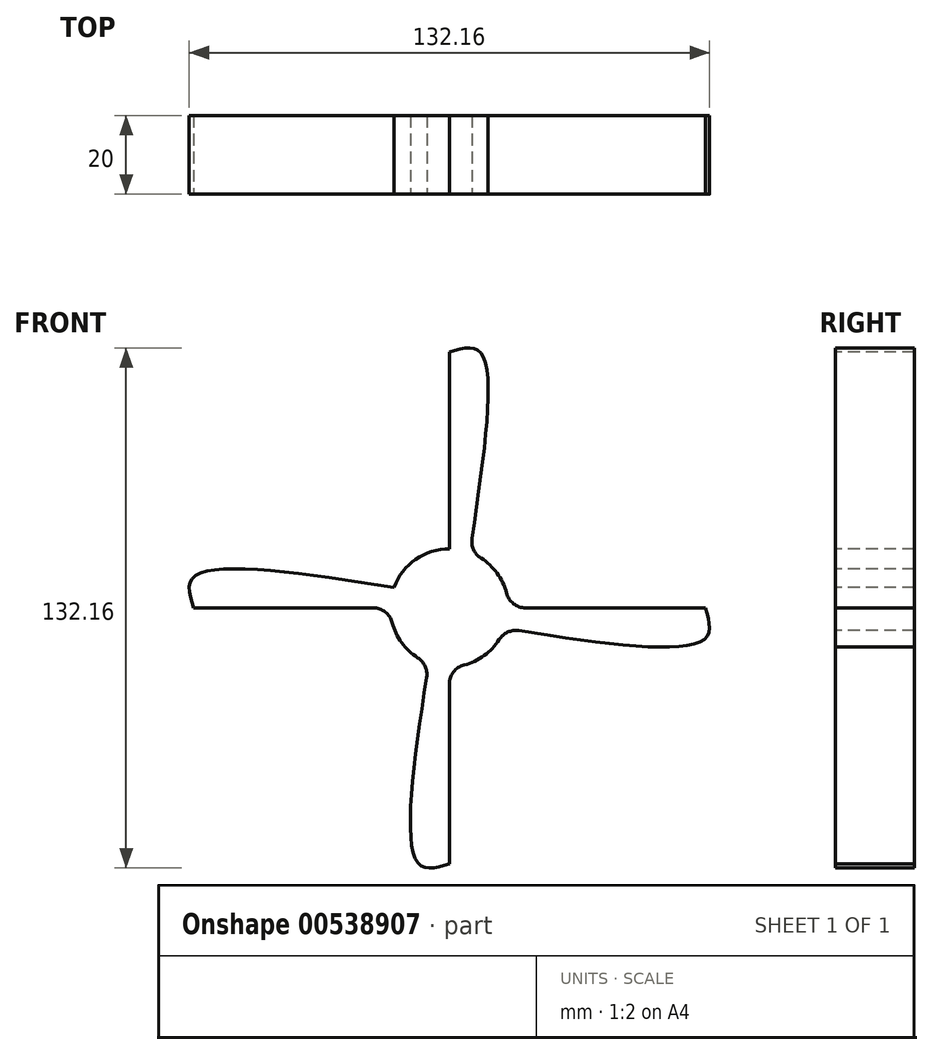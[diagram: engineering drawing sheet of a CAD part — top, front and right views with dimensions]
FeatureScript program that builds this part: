
annotation { "Feature Type Name" : "Feature", "Feature Type Description" : "" }
export const myFeature = defineFeature(function(context is Context, id is Id, definition is map)
    precondition{}
    {
        {
            var Q0;
            Q0=qCreatedBy(makeId("Front.planeOp"),FACE);
            var sketch = newSketch(context, id + "F0", { "sketchPlane" : qUnion([Q0])});
            skCircle(sketch, "E0", {"center": v(0, 0) * mm, "radius": 15 * mm});
            skSolve(sketch);
        }
        {
            var Q0;
            Q0 = qSketchRegion(id + "F0", true);
            extrude(context, id + "F1", {"entities" : qUnion([Q0]), "depth" : 20 * mm, "offsetDistance" : 25 * mm});
        }
        {
            var Q0;
            Q0=makeQuery(id+"F1.opExtrude","CAP_FACE",FACE,{"disambiguationData":[OSD([sQuery(id+"F0.wireOp",EDGE,"E0")])],"isStart":false});
            var sketch = newSketch(context, id + "F2", { "sketchPlane" : qUnion([Q0])});
            skLineSegment(sketch, "E1", {"start": v(0, 15) * mm, "end": v(0, 65) * mm});
            skLineSegment(sketch, "E2", {"start": v(15, 0) * mm, "end": v(65, 0) * mm});
            skLineSegment(sketch, "E3", {"start": v(0, -15) * mm, "end": v(0, -65) * mm});
            skLineSegment(sketch, "E4", {"start": v(-15, 0) * mm, "end": v(-65, 0) * mm});
            skFitSpline(sketch, "E5", {"points": [v(0, -65) * mm, v(-7.8, -65) * mm, v(-5.23, -14.06) * mm], "startDerivative": vector(-32.14, -9.96) * mm, "endDerivative": vector(14.83, 96.32) * mm});
            skPoint(sketch, "E6.2.internal.snap0", {"position": v(-65, 3.9) * mm});
            skFitSpline(sketch, "E7", {"points": [v(0, 65) * mm, v(7.8, 65) * mm, v(5.23, 14.06) * mm], "startDerivative": vector(32.07, 9.98) * mm, "endDerivative": vector(-13.87, -96.7) * mm});
            skFitSpline(sketch, "E8", {"points": [v(65, 0) * mm, v(65, -7.8) * mm, v(14.06, -5.23) * mm], "startDerivative": vector(9.95, -32.18) * mm, "endDerivative": vector(-96.14, 15.45) * mm});
            skFitSpline(sketch, "E9", {"points": [v(-65, 0) * mm, v(-65, 7.8) * mm, v(-14.06, 5.23) * mm], "startDerivative": vector(-9.96, 32.14) * mm, "endDerivative": vector(96.33, -14.83) * mm});
            skLineSegment(sketch, "E10", {"start": v(-14.06, 5.23) * mm, "end": v(-15, 0) * mm});
            skLineSegment(sketch, "E11", {"start": v(0, 15) * mm, "end": v(5.23, 14.06) * mm});
            skLineSegment(sketch, "E12", {"start": v(15, 0) * mm, "end": v(14.06, -5.23) * mm});
            skLineSegment(sketch, "E13", {"start": v(0, -15) * mm, "end": v(-5.23, -14.06) * mm});
            skSolve(sketch);
        }
        {
            var Q0;
            {var subQ0=sQuery(id+"F2.wireOp",EDGE,"E4");Q0=makeQuery(id+"F2.imprint","IMPRINT",FACE,{"disambiguationData":[TD([[makeQuery(id+"F2.imprint","IMPRINT",EDGE,{"derivedFrom":subQ0}),-1.0]])]});}
            var Q1;
            {var subQ0=sQuery(id+"F2.wireOp",EDGE,"E1");Q1=makeQuery(id+"F2.imprint","IMPRINT",FACE,{"disambiguationData":[TD([[makeQuery(id+"F2.imprint","IMPRINT",EDGE,{"derivedFrom":subQ0}),-1.0]])]});}
            var Q2;
            {var subQ0=sQuery(id+"F2.wireOp",EDGE,"E2");Q2=makeQuery(id+"F2.imprint","IMPRINT",FACE,{"disambiguationData":[TD([[makeQuery(id+"F2.imprint","IMPRINT",EDGE,{"derivedFrom":subQ0}),-1.0]])]});}
            var Q3;
            {var subQ0=sQuery(id+"F2.wireOp",EDGE,"E3");Q3=makeQuery(id+"F2.imprint","IMPRINT",FACE,{"disambiguationData":[TD([[makeQuery(id+"F2.imprint","IMPRINT",EDGE,{"derivedFrom":subQ0}),-1.0]])]});}
            extrude(context, id + "F3", {"entities" : qUnion([Q0, Q1, Q2, Q3]), "operationType" : NewBodyOperationType.ADD, "oppositeDirection" : true, "depth" : 20 * mm, "offsetDistance" : 25 * mm});
        }
        {
            var Q0;
            Q0=makeQuery(id+"F3.opExtrude","SWEPT_EDGE",EDGE,{"disambiguationData":[OSD([sQuery(id+"F0.wireOp",EDGE,"E0"),sQuery(id+"F2.wireOp",EDGE,"E1"),sQuery(id+"F2.wireOp",EDGE,"E11")])]});
            var Q1;
            Q1=makeQuery(id+"F3.opExtrude","SWEPT_EDGE",EDGE,{"disambiguationData":[OSD([sQuery(id+"F0.wireOp",EDGE,"E0"),sQuery(id+"F2.wireOp",EDGE,"E9"),sQuery(id+"F2.wireOp",EDGE,"E10")])]});
            var Q2;
            Q2=makeQuery(id+"F3.opExtrude","SWEPT_EDGE",EDGE,{"disambiguationData":[OSD([sQuery(id+"F0.wireOp",EDGE,"E0"),sQuery(id+"F2.wireOp",EDGE,"E4"),sQuery(id+"F2.wireOp",EDGE,"E10")])]});
            var Q3;
            Q3=makeQuery(id+"F3.opExtrude","SWEPT_EDGE",EDGE,{"disambiguationData":[OSD([sQuery(id+"F0.wireOp",EDGE,"E0"),sQuery(id+"F2.wireOp",EDGE,"E5"),sQuery(id+"F2.wireOp",EDGE,"E13")])]});
            var Q4;
            Q4=makeQuery(id+"F3.opExtrude","SWEPT_EDGE",EDGE,{"disambiguationData":[OSD([sQuery(id+"F0.wireOp",EDGE,"E0"),sQuery(id+"F2.wireOp",EDGE,"E3"),sQuery(id+"F2.wireOp",EDGE,"E13")])]});
            var Q5;
            Q5=makeQuery(id+"F3.opExtrude","SWEPT_EDGE",EDGE,{"disambiguationData":[OSD([sQuery(id+"F0.wireOp",EDGE,"E0"),sQuery(id+"F2.wireOp",EDGE,"E8"),sQuery(id+"F2.wireOp",EDGE,"E12")])]});
            var Q6;
            Q6=makeQuery(id+"F3.opExtrude","SWEPT_EDGE",EDGE,{"disambiguationData":[OSD([sQuery(id+"F0.wireOp",EDGE,"E0"),sQuery(id+"F2.wireOp",EDGE,"E7"),sQuery(id+"F2.wireOp",EDGE,"E11")])]});
            var Q7;
            Q7=makeQuery(id+"F3.opExtrude","SWEPT_EDGE",EDGE,{"disambiguationData":[OSD([sQuery(id+"F0.wireOp",EDGE,"E0"),sQuery(id+"F2.wireOp",EDGE,"E2"),sQuery(id+"F2.wireOp",EDGE,"E12")])]});
            fillet(context, id + "F4", {"entities" : qUnion([Q0, Q1, Q2, Q3, Q4, Q5, Q6, Q7]), "radius" : 5 * mm, "tangentPropagation" : true, "allowEdgeOverflow" : false});
        }
    });
